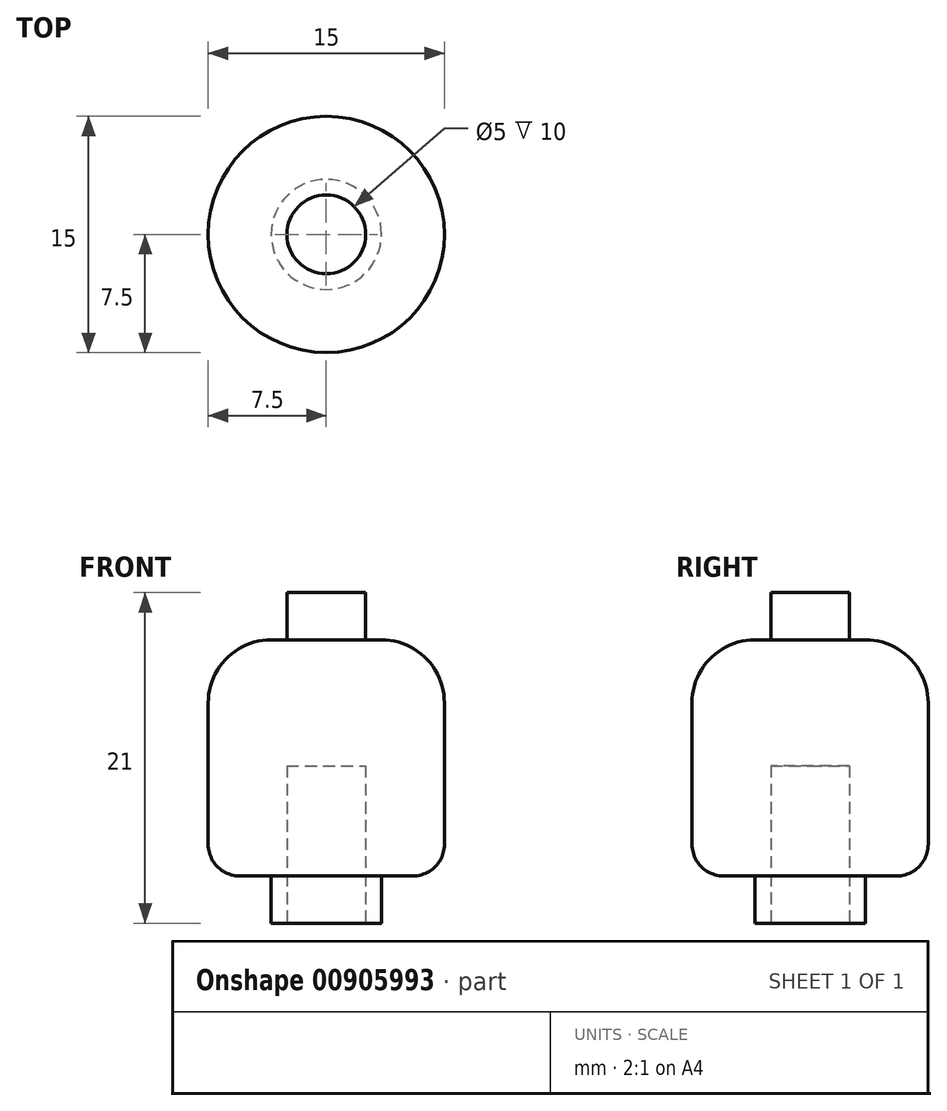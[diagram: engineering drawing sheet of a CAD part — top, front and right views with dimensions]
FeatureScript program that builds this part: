
annotation { "Feature Type Name" : "Feature", "Feature Type Description" : "" }
export const myFeature = defineFeature(function(context is Context, id is Id, definition is map)
    precondition{}
    {
        {
            var Q0;
            Q0=qCreatedBy(makeId("Top.planeOp"),FACE);
            var sketch = newSketch(context, id + "F0", { "sketchPlane" : qUnion([Q0])});
            skCircle(sketch, "E0", {"center": v(0, 0) * mm, "radius": 3.5 * mm});
            skSolve(sketch);
        }
        {
            var Q0;
            Q0=makeQuery(id+"F0.imprint","IMPRINT",FACE,{"disambiguationData":[TD([[makeQuery(id+"F0.imprint","IMPRINT",EDGE,{"derivedFrom":sQuery(id+"F0.wireOp",EDGE,"E0")}),1.0]])]});
            extrude(context, id + "F1", {"entities" : qUnion([Q0]), "depth" : 3 * mm, "offsetDistance" : 25.4 * mm});
        }
        {
            var Q0;
            Q0=makeQuery(id+"F1.opExtrude","CAP_FACE",FACE,{"disambiguationData":[OSD([sQuery(id+"F0.wireOp",EDGE,"E0")])],"isStart":false});
            var sketch = newSketch(context, id + "F2", { "sketchPlane" : qUnion([Q0])});
            skCircle(sketch, "E1", {"center": v(0, 0) * mm, "radius": 7.5 * mm});
            skSolve(sketch);
        }
        {
            var Q0;
            Q0=makeQuery(id+"F2.imprint","IMPRINT",FACE,{"disambiguationData":[TD([[makeQuery(id+"F2.imprint","IMPRINT",EDGE,{"derivedFrom":makeQuery(id+"F1.opExtrude","CAP_EDGE",EDGE,{"disambiguationData":[OSD([sQuery(id+"F0.wireOp",EDGE,"E0")])],"isStart":false})}),1.0]])]});
            var Q1;
            Q1=makeQuery(id+"F2.imprint","IMPRINT",FACE,{"disambiguationData":[TD([[makeQuery(id+"F2.imprint","IMPRINT",EDGE,{"derivedFrom":sQuery(id+"F2.wireOp",EDGE,"E1")}),1.0]])]});
            extrude(context, id + "F3", {"entities" : qUnion([Q0, Q1]), "operationType" : NewBodyOperationType.ADD, "depth" : 15 * mm, "offsetDistance" : 25.4 * mm});
        }
        {
            var Q0;
            Q0=makeQuery(id+"F3.opExtrude","CAP_FACE",FACE,{"disambiguationData":[OSD([sQuery(id+"F2.wireOp",EDGE,"E1")])],"isStart":false});
            var sketch = newSketch(context, id + "F4", { "sketchPlane" : qUnion([Q0])});
            skCircle(sketch, "E2", {"center": v(0, 0) * mm, "radius": 2.5 * mm});
            skSolve(sketch);
        }
        {
            var Q0;
            Q0=makeQuery(id+"F4.imprint","IMPRINT",FACE,{"disambiguationData":[TD([[makeQuery(id+"F4.imprint","IMPRINT",EDGE,{"derivedFrom":sQuery(id+"F4.wireOp",EDGE,"E2")}),1.0]])]});
            extrude(context, id + "F5", {"entities" : qUnion([Q0]), "operationType" : NewBodyOperationType.ADD, "depth" : 3 * mm, "offsetDistance" : 25.4 * mm});
        }
        {
            var Q0;
            Q0=makeQuery(id+"F1.opExtrude","CAP_FACE",FACE,{"disambiguationData":[OSD([sQuery(id+"F0.wireOp",EDGE,"E0")])],"isStart":true});
            var sketch = newSketch(context, id + "F6", { "sketchPlane" : qUnion([Q0])});
            skCircle(sketch, "E3", {"center": v(0, 0) * mm, "radius": 2.5 * mm});
            skSolve(sketch);
        }
        {
            var Q0;
            Q0=makeQuery(id+"F6.imprint","IMPRINT",FACE,{"disambiguationData":[TD([[makeQuery(id+"F6.imprint","IMPRINT",EDGE,{"derivedFrom":sQuery(id+"F6.wireOp",EDGE,"E3")}),1.0]])]});
            extrude(context, id + "F7", {"entities" : qUnion([Q0]), "operationType" : NewBodyOperationType.REMOVE, "oppositeDirection" : true, "depth" : 10 * mm, "offsetDistance" : 25.4 * mm});
        }
        {
            var Q0;
            Q0=makeQuery(id+"F3.opExtrude","CAP_EDGE",EDGE,{"disambiguationData":[OSD([sQuery(id+"F2.wireOp",EDGE,"E1")])],"isStart":false});
            fillet(context, id + "F8", {"entities" : qUnion([Q0]), "radius" : 4 * mm, "tangentPropagation" : true, "allowEdgeOverflow" : false});
        }
        {
            var Q0;
            Q0=makeQuery(id+"F3.opExtrude","CAP_EDGE",EDGE,{"disambiguationData":[OSD([sQuery(id+"F2.wireOp",EDGE,"E1")])],"isStart":true});
            fillet(context, id + "F9", {"entities" : qUnion([Q0]), "radius" : 2 * mm, "tangentPropagation" : true, "allowEdgeOverflow" : false});
        }
    });
